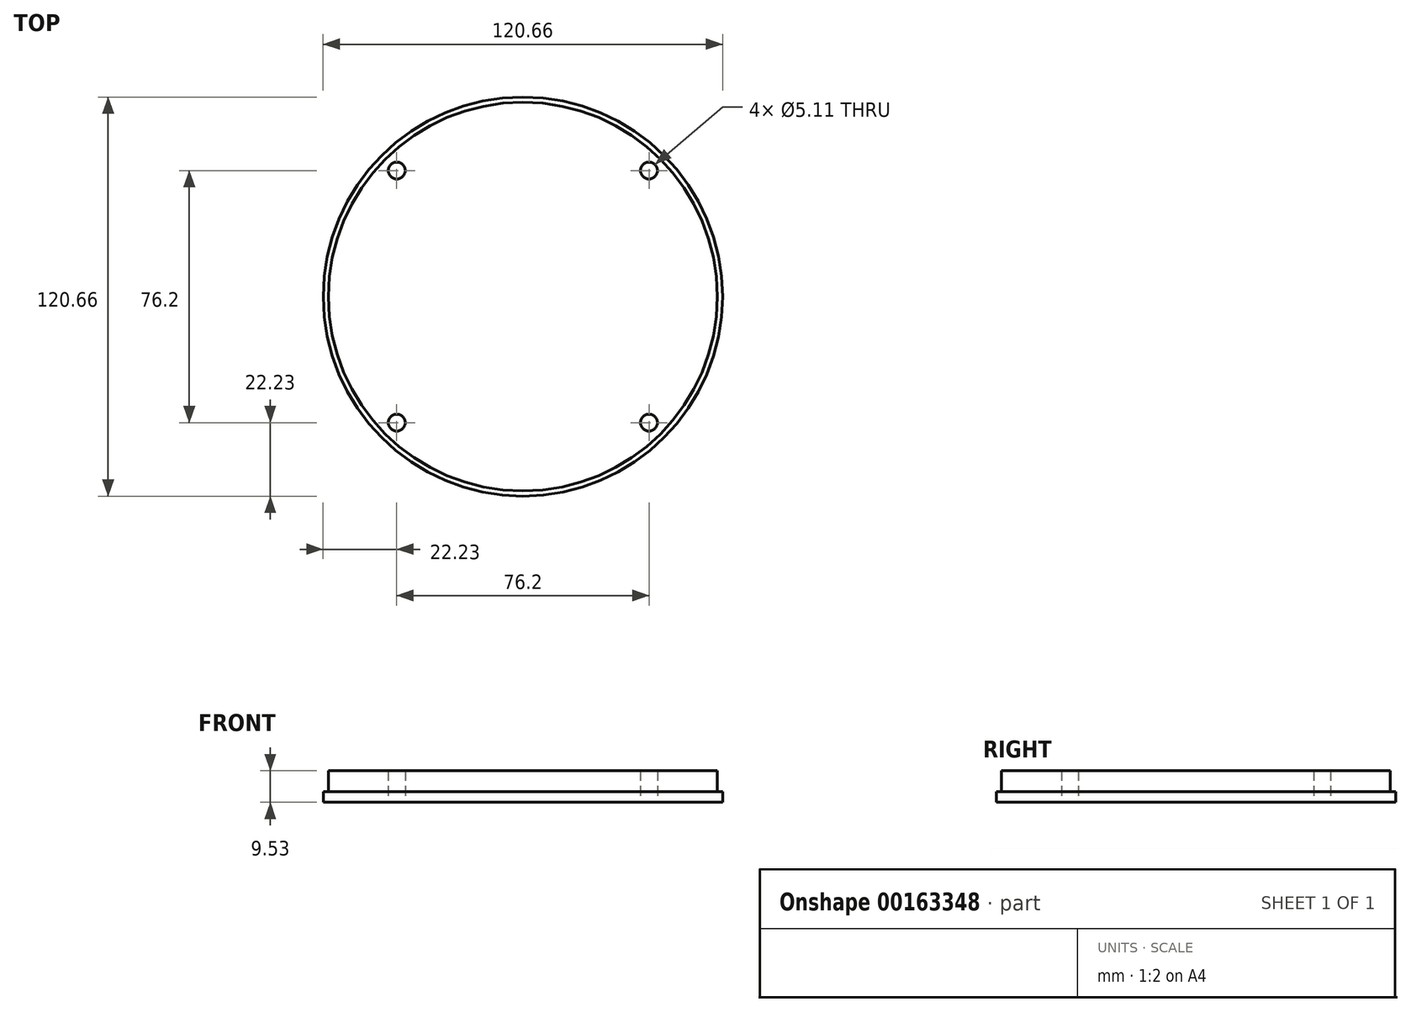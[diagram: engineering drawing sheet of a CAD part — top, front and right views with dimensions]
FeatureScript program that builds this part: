
annotation { "Feature Type Name" : "Feature", "Feature Type Description" : "" }
export const myFeature = defineFeature(function(context is Context, id is Id, definition is map)
    precondition{}
    {
        {
            var Q0;
            Q0=qCreatedBy(makeId("Top.planeOp"),FACE);
            var sketch = newSketch(context, id + "F0", { "sketchPlane" : qUnion([Q0])});
            skCircle(sketch, "E0", {"center": v(0, 0) * mm, "radius": 58.74 * mm});
            skCircle(sketch, "E1", {"center": v(0, 0) * mm, "radius": 60.33 * mm});
            skPoint(sketch, "E2.right.start.orphan", {"position": v(-38.1, 38.1) * mm});
            skPoint(sketch, "E2.left.start.orphan", {"position": v(38.1, 38.1) * mm});
            skPoint(sketch, "E2.top.end.orphan", {"position": v(-38.1, -38.1) * mm});
            skPoint(sketch, "E2.top.start.orphan", {"position": v(38.1, -38.1) * mm});
            skSolve(sketch);
        }
        {
            var Q0;
            Q0=makeQuery(id+"F0.imprint","IMPRINT",FACE,{"disambiguationData":[TD([[makeQuery(id+"F0.imprint","IMPRINT",EDGE,{"derivedFrom":sQuery(id+"F0.wireOp",EDGE,"E0")}),1.0]])]});
            var Q1;
            Q1=makeQuery(id+"F0.imprint","IMPRINT",FACE,{"disambiguationData":[TD([[makeQuery(id+"F0.imprint","IMPRINT",EDGE,{"derivedFrom":sQuery(id+"F0.wireOp",EDGE,"E2.bottom")}),1.0]])]});
            var Q2;
            Q2=makeQuery(id+"F0.imprint","IMPRINT",FACE,{"disambiguationData":[TD([[makeQuery(id+"F0.imprint","IMPRINT",EDGE,{"derivedFrom":sQuery(id+"F0.wireOp",EDGE,"E0")}),-1.0]])]});
            extrude(context, id + "F1", {"entities" : qUnion([Q0, Q1, Q2]), "depth" : 3.17 * mm});
        }
        {
            var Q0;
            Q0=makeQuery(id+"F0.imprint","IMPRINT",FACE,{"disambiguationData":[TD([[makeQuery(id+"F0.imprint","IMPRINT",EDGE,{"derivedFrom":sQuery(id+"F0.wireOp",EDGE,"E0")}),1.0]])]});
            extrude(context, id + "F2", {"entities" : qUnion([Q0]), "operationType" : NewBodyOperationType.ADD, "depth" : 9.52 * mm});
        }
        {
            var Q0;
            Q0=sQuery(id+"F0.wireOp",VERTEX,"E2.left.start.orphan");
            var Q1;
            Q1=sQuery(id+"F0.wireOp",VERTEX,"E2.right.start.orphan");
            var Q2;
            Q2=sQuery(id+"F0.wireOp",VERTEX,"E2.top.end.orphan");
            var Q3;
            Q3=sQuery(id+"F0.wireOp",VERTEX,"E2.top.start.orphan");
            var Q4;
            Q4=makeQuery(id+"F1.opExtrude","SWEPT_BODY",BODY,{"disambiguationData":[OSD([sQuery(id+"F0.wireOp",EDGE,"E1")])]});
            hole(context, id + "F3", {"style" : HoleStyle.SIMPLE, "endStyle" : HoleEndStyle.BLIND, "oppositeDirection" : true, "holeDiameter" : 5.1 * mm, "holeDepth" : 76.2 * mm, "locations" : qUnion([Q0, Q1, Q2, Q3]), "scope" : qUnion([Q4])});
        }
    });
